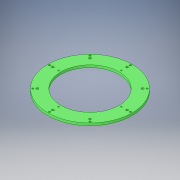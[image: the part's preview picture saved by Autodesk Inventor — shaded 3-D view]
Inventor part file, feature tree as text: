
AUTODESK INVENTOR PART (.ipt)
format: ipt  version: 2016 SP1 (Build 200210100, 210)  size: 156,160 bytes
history: native  units: in
note: dims shown in document units (in); Inventor stores cm internally (conversion verified against a paired STEP export)
features: hole x1, pattern_circular x1, sketch x1, other x1
ambient origin geometry x8: Origin, YZ Plane, XZ Plane, XY Plane, X Axis, Y Axis, Z Axis, Center Point
bodies: Solid1 (feature_tree)
feature tree (4):
  hole  "Hole6"  [1 undecoded]
  pattern_circular  "Circular Pattern9"  [2 undecoded]
  sketch  "Sketch10"  dims[d70=5.75in d71=0.332in d72=0.75in d73=0.635in d74=0.25in d75=0.5635in d76=1.0in d77=0.8108in d78=3.1496in d79=360.0deg]
  parser-record x1  (decoder bookkeeping rows leaked as tree rows — omitted from the tree; the rows remain in map.json)
note: 3 required parameter values undecoded (feature->parameter linkage not recoverable at this tier; creation-order binding heuristic only, values carry confidence <= 0.55)
